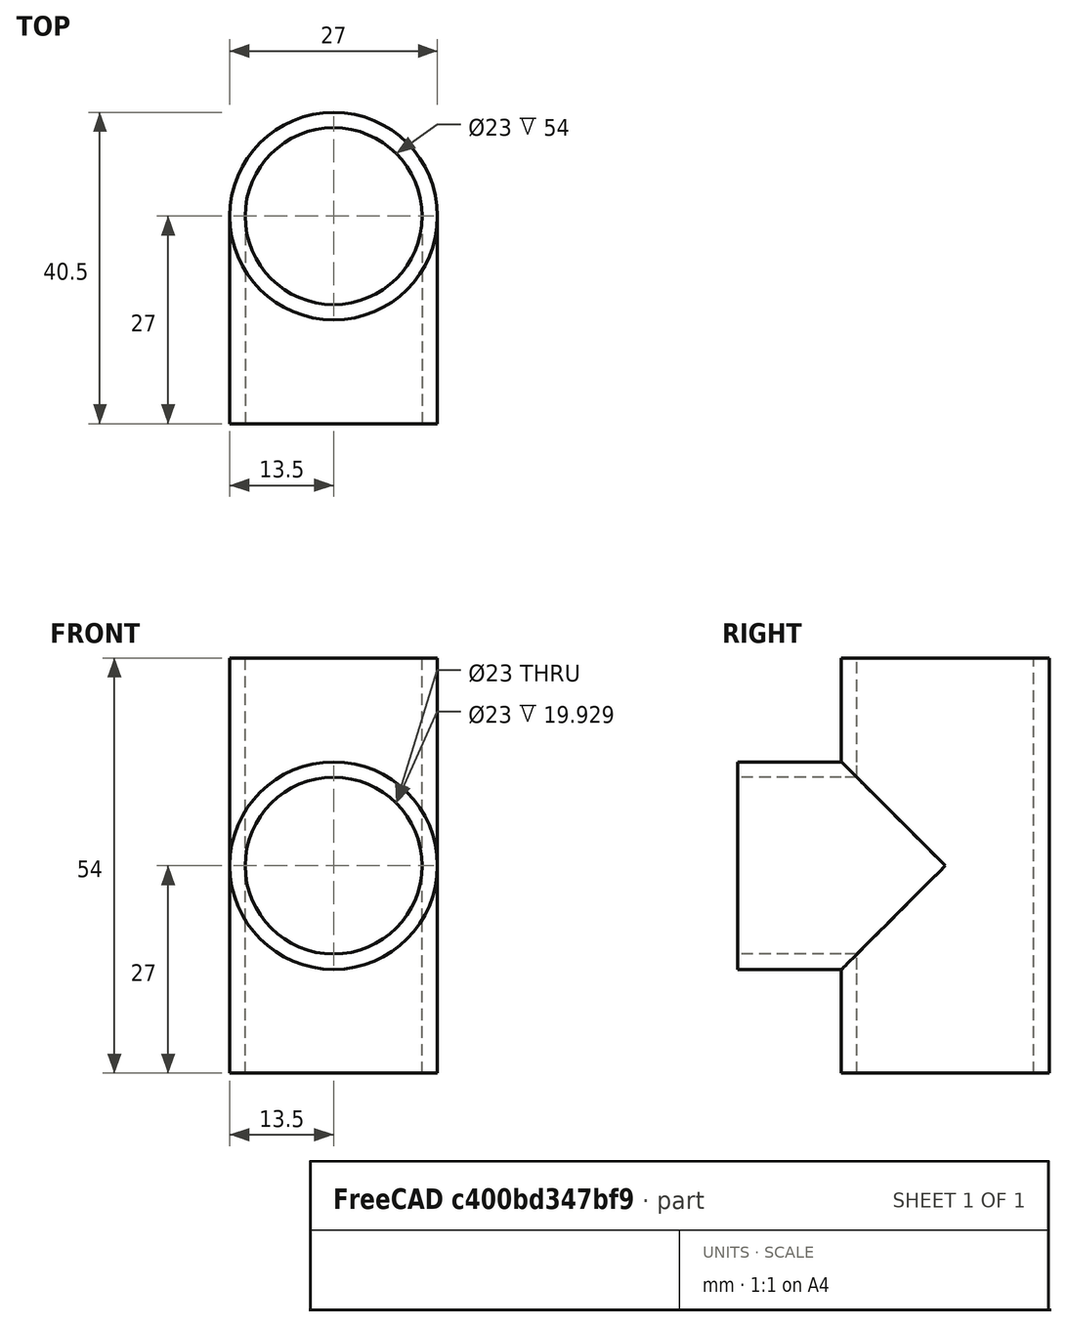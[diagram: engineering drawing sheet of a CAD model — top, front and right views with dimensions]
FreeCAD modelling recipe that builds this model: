
FCSTD DOCUMENT  (FreeCAD 0.16R5914 (Git))
Label: FIG_130_DN15
License: All rights reserved
LicenseURL: http://en.wikipedia.org/wiki/All_rights_reserved
objects: Part::Cylinder×2, Part::Thickness×2, Part::FeaturePython×1
note: 5 computed .brp shape members not serialized (recipe doc carries the construction recipe); baked Part::Feature solids carry a one-line shape summary decoded from their .brp

FEATURE [Part::Cylinder] Cylinder  label="Cilindro"
  Angle = 360
  Height = 54
  Radius = 13.5
FEATURE [Part::Thickness] Thickness
  Faces = -> Cylinder [Face3,Face2]
  Intersection = false
  Join = 2
  Mode = 1
  SelfIntersection = false
  Value = -2
FEATURE [Part::Cylinder] Cylinder001  label="Cilindro001"
  Angle = 360
  Height = 27
  Placement = pos=(0,0,0) rot=(1,0,0;1.5708rad)
  Radius = 13.5
FEATURE [Part::Thickness] Thickness001
  Faces = -> Cylinder001 [Face2,Face3]
  Intersection = false
  Join = 2
  Mode = 1
  Placement = pos=(0,0,27) rot=(0,0,1;0rad)
  SelfIntersection = false
  Value = -2
FEATURE [Part::FeaturePython] Connect  # WARN: FeaturePython — macro-defined, semantics opaque (R4)
  Base = -> Thickness
  Mode = 1
  Tool = -> Thickness001
